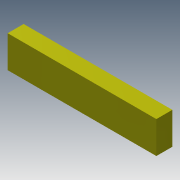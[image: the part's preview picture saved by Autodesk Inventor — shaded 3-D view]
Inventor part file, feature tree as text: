
AUTODESK INVENTOR PART (.ipt)
format: ipt  version: 2013 (Build 170138000, 138)  size: 71,680 bytes
history: native  units: mm
features: extrude x1, sketch x1
ambient origin geometry x8: Origin, YZ Plane, XZ Plane, XY Plane, X Axis, Y Axis, Z Axis, Center Point
bodies: Solid1 (feature_tree)
feature tree (2):
  extrude  "Extrusion1"  Depth=20.0mm
  sketch  "Sketch1"  dims[d0=93.0mm d1=20.0mm d2=10.0mm d3=0.0mm]
